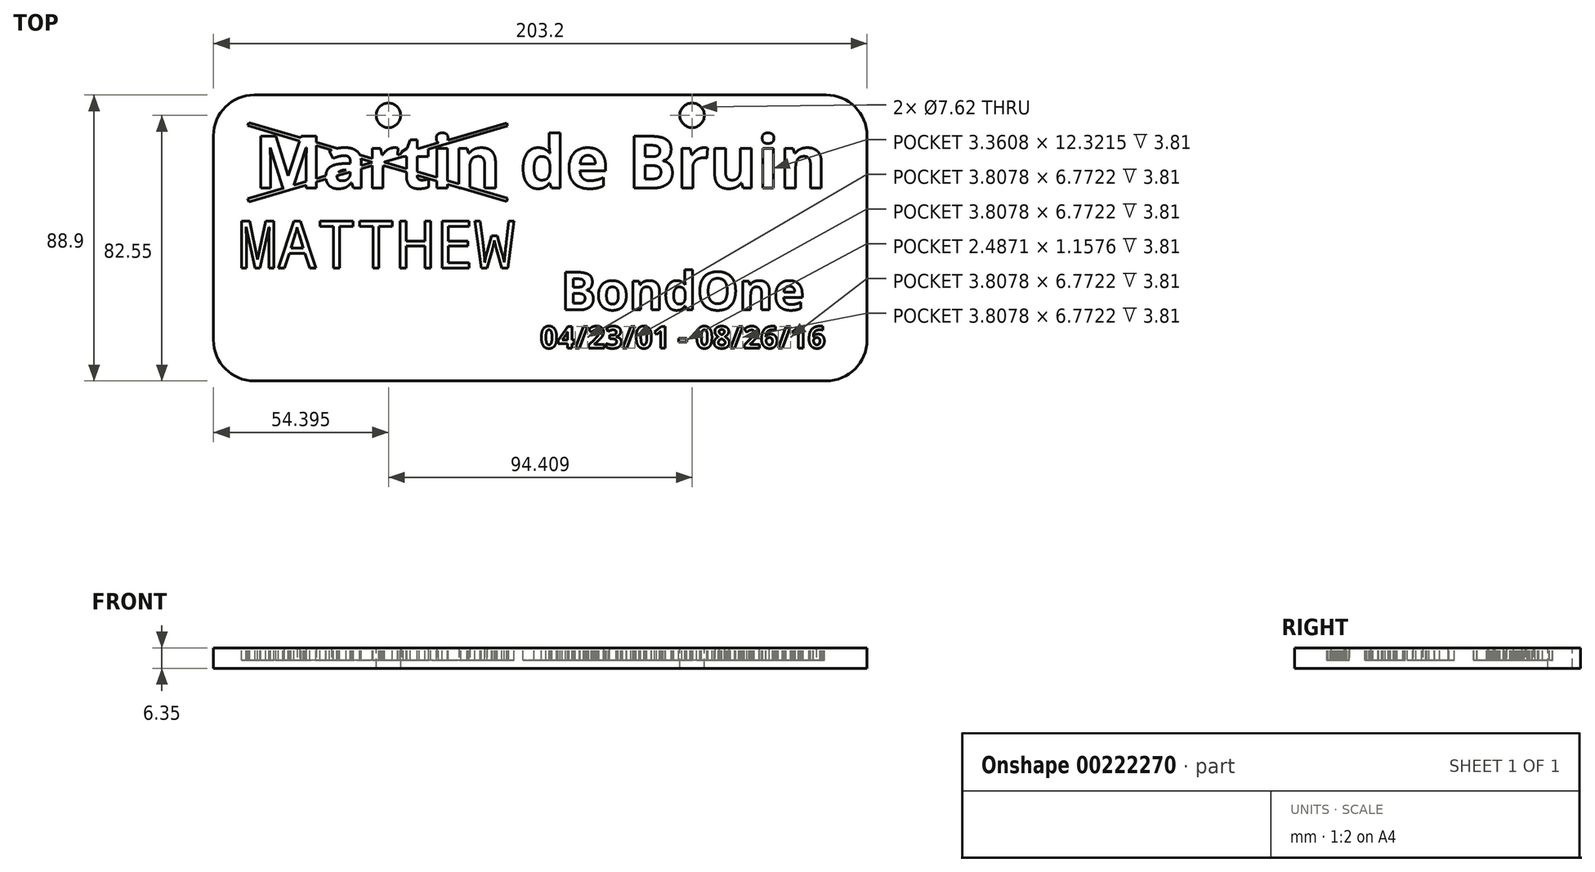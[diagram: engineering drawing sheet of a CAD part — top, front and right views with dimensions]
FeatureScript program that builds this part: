
annotation { "Feature Type Name" : "Feature", "Feature Type Description" : "" }
export const myFeature = defineFeature(function(context is Context, id is Id, definition is map)
    precondition{}
    {
        {
            var Q0;
            Q0=qCreatedBy(makeId("Top.planeOp"),FACE);
            var sketch = newSketch(context, id + "F0", { "sketchPlane" : qUnion([Q0])});
            skLineSegment(sketch, "E0.bottom", {"start": v(-101.6, 44.45) * mm, "end": v(101.6, 44.45) * mm});
            skLineSegment(sketch, "E0.top", {"start": v(-101.6, -44.45) * mm, "end": v(101.6, -44.45) * mm});
            skLineSegment(sketch, "E0.left", {"start": v(-101.6, 44.45) * mm, "end": v(-101.6, -44.45) * mm});
            skLineSegment(sketch, "E0.right", {"start": v(101.6, 44.45) * mm, "end": v(101.6, -44.45) * mm});
            skSolve(sketch);
        }
        {
            var Q0;
            Q0=makeQuery(id+"F0.imprint","IMPRINT",FACE,{"disambiguationData":[TD([[makeQuery(id+"F0.imprint","IMPRINT",EDGE,{"derivedFrom":sQuery(id+"F0.wireOp",EDGE,"E0.bottom")}),-1.0]])]});
            extrude(context, id + "F1", {"entities" : qUnion([Q0]), "depth" : 6.35 * mm});
        }
        {
            var Q0;
            Q0=makeQuery(id+"F1.opExtrude","CAP_FACE",FACE,{"disambiguationData":[OSD([sQuery(id+"F0.wireOp",EDGE,"E0.bottom"),sQuery(id+"F0.wireOp",EDGE,"E0.top"),sQuery(id+"F0.wireOp",EDGE,"E0.left"),sQuery(id+"F0.wireOp",EDGE,"E0.right")])],"isStart":false});
            var sketch = newSketch(context, id + "F2", { "sketchPlane" : qUnion([Q0])});
            skText(sketch, "E1", { "text": "Martin de Bruin", "fontName": "OpenSans-Bold.ttf"});
            skText(sketch, "E2", { "text": "04/23/01 - 08/26/16", "fontName": "OpenSans-Bold.ttf"});
            skText(sketch, "E3", { "text": "MATTHEW", "fontName": "DroidSansMono.ttf"});
            skText(sketch, "E4", { "text": "BondOne", "fontName": "OpenSans-Bold.ttf"});
            const initialGuessF2  = {"E1": [-0.0889, 0.0155, 1, 0, 0.01625], "E2": [0, -0.03429, 1, 0, 0.00683], "E3": [-0.09398, -0.00938, 1, 0, 0.01471], "E4": [0.00635, -0.02238, 1, 0, 0.0118]};
            skSetInitialGuess(sketch, initialGuessF2);
            skSolve(sketch);
        }
        {
            var Q0;
            Q0 = qSketchRegion(id + "F2", true);
            extrude(context, id + "F3", {"entities" : qUnion([Q0]), "operationType" : NewBodyOperationType.REMOVE, "oppositeDirection" : true, "depth" : 3.8 * mm});
        }
        {
            var Q0;
            Q0=makeQuery(id+"F1.opExtrude","SWEPT_EDGE",EDGE,{"disambiguationData":[OSD([sQuery(id+"F0.wireOp",EDGE,"E0.bottom"),sQuery(id+"F0.wireOp",EDGE,"E0.left")])]});
            var Q1;
            Q1=makeQuery(id+"F1.opExtrude","SWEPT_EDGE",EDGE,{"disambiguationData":[OSD([sQuery(id+"F0.wireOp",EDGE,"E0.bottom"),sQuery(id+"F0.wireOp",EDGE,"E0.right")])]});
            var Q2;
            Q2=makeQuery(id+"F1.opExtrude","SWEPT_EDGE",EDGE,{"disambiguationData":[OSD([sQuery(id+"F0.wireOp",EDGE,"E0.top"),sQuery(id+"F0.wireOp",EDGE,"E0.right")])]});
            var Q3;
            Q3=makeQuery(id+"F1.opExtrude","SWEPT_EDGE",EDGE,{"disambiguationData":[OSD([sQuery(id+"F0.wireOp",EDGE,"E0.top"),sQuery(id+"F0.wireOp",EDGE,"E0.left")])]});
            fillet(context, id + "F4", {"entities" : qUnion([Q0, Q1, Q2, Q3]), "radius" : 12.7 * mm, "tangentPropagation" : true, "allowEdgeOverflow" : false});
        }
        {
            var Q0;
            {var subQ0=sQuery(id+"F0.wireOp",EDGE,"E0.top");var subQ1=sQuery(id+"F0.wireOp",EDGE,"E0.left");var subQ2=sQuery(id+"F0.wireOp",EDGE,"E0.bottom");var subQ3=sQuery(id+"F0.wireOp",EDGE,"E0.right");Q0=makeQuery(id+"F3.boolean.opBoolean","SPLIT",FACE,{"disambiguationData":[TD([makeQuery(id+"F1.opExtrude","SWEPT_FACE",FACE,{"disambiguationData":[OSD([subQ2])]})])],"derivedFrom":makeQuery(id+"F1.opExtrude","CAP_FACE",FACE,{"disambiguationData":[OSD([subQ2,subQ0,subQ1,subQ3])],"isStart":false})});}
            var sketch = newSketch(context, id + "F5", { "sketchPlane" : qUnion([Q0])});
            skCircle(sketch, "E5", {"center": v(-47.2, 38.1) * mm, "radius": 3.81 * mm});
            skCircle(sketch, "E6", {"center": v(47.2, 38.1) * mm, "radius": 3.81 * mm});
            skSolve(sketch);
        }
        {
            var Q0;
            Q0=makeQuery(id+"F5.imprint","IMPRINT",FACE,{"disambiguationData":[TD([[makeQuery(id+"F5.imprint","IMPRINT",EDGE,{"derivedFrom":sQuery(id+"F5.wireOp",EDGE,"E5")}),1.0]])]});
            var Q1;
            Q1=makeQuery(id+"F5.imprint","IMPRINT",FACE,{"disambiguationData":[TD([[makeQuery(id+"F5.imprint","IMPRINT",EDGE,{"derivedFrom":sQuery(id+"F5.wireOp",EDGE,"E6")}),1.0]])]});
            extrude(context, id + "F6", {"entities" : qUnion([Q0, Q1]), "operationType" : NewBodyOperationType.REMOVE, "oppositeDirection" : true, "depth" : 25.4 * mm});
        }
        {
            var Q0;
            {var subQ0=sQuery(id+"F0.wireOp",EDGE,"E0.top");var subQ1=sQuery(id+"F0.wireOp",EDGE,"E0.left");var subQ2=sQuery(id+"F0.wireOp",EDGE,"E0.bottom");var subQ3=sQuery(id+"F0.wireOp",EDGE,"E0.right");Q0=makeQuery(id+"F3.boolean.opBoolean","SPLIT",FACE,{"disambiguationData":[TD([makeQuery(id+"F1.opExtrude","SWEPT_FACE",FACE,{"disambiguationData":[OSD([subQ2])]})])],"derivedFrom":makeQuery(id+"F1.opExtrude","CAP_FACE",FACE,{"disambiguationData":[OSD([subQ2,subQ0,subQ1,subQ3])],"isStart":false})});}
            var sketch = newSketch(context, id + "F7", { "sketchPlane" : qUnion([Q0])});
            skLineSegment(sketch, "E7.bottom", {"start": v(-90.93, 35.42) * mm, "end": v(-9.84, 35.42) * mm});
            skLineSegment(sketch, "E7.top", {"start": v(-90.93, 11.69) * mm, "end": v(-9.84, 11.69) * mm});
            skLineSegment(sketch, "E7.left", {"start": v(-90.93, 35.42) * mm, "end": v(-90.93, 11.69) * mm});
            skLineSegment(sketch, "E7.right", {"start": v(-9.84, 35.42) * mm, "end": v(-9.84, 11.69) * mm});
            skLineSegment(sketch, "E8", {"start": v(-90.93, 11.69) * mm, "end": v(-9.84, 35.42) * mm});
            skLineSegment(sketch, "E9", {"start": v(-9.84, 11.69) * mm, "end": v(-90.93, 35.42) * mm});
            skLineSegment(sketch, "E10", {"start": v(-90.93, 12.21) * mm, "end": v(-10.49, 35.76) * mm});
            skLineSegment(sketch, "E11", {"start": v(-10.49, 35.76) * mm, "end": v(-10.2, 34.79) * mm});
            skLineSegment(sketch, "E12", {"start": v(-10.2, 34.79) * mm, "end": v(-90.64, 11.24) * mm});
            skLineSegment(sketch, "E13", {"start": v(-90.64, 11.24) * mm, "end": v(-90.97, 12.34) * mm});
            skLineSegment(sketch, "E14", {"start": v(-90.93, 12.21) * mm, "end": v(-90.93, 12.21) * mm});
            skLineSegment(sketch, "E15", {"start": v(-90.93, 34.9) * mm, "end": v(-10.49, 11.35) * mm});
            skLineSegment(sketch, "E16", {"start": v(-10.49, 11.35) * mm, "end": v(-10.2, 12.32) * mm});
            skLineSegment(sketch, "E17", {"start": v(-10.2, 12.32) * mm, "end": v(-90.64, 35.87) * mm});
            skLineSegment(sketch, "E18", {"start": v(-90.64, 35.87) * mm, "end": v(-90.94, 34.86) * mm});
            skLineSegment(sketch, "E19", {"start": v(-90.93, 34.9) * mm, "end": v(-90.93, 34.9) * mm});
            skSolve(sketch);
        }
        {
            var Q0;
            {var subQ0=sQuery(id+"F7.wireOp",EDGE,"E18");var subQ1=sQuery(id+"F7.wireOp",EDGE,"E7.bottom");var subQ2=makeQuery(id+"F7.imprint","INTERSECT",VERTEX,{"derivedFrom":[subQ1,subQ0]});Q0=makeQuery(id+"F7.imprint","IMPRINT",FACE,{"disambiguationData":[TD([[makeQuery(id+"F7.imprint","IMPRINT",EDGE,{"disambiguationData":[TD([[subQ2,-1.0]])],"derivedFrom":subQ1}),-1.0]])]});}
            var Q1;
            {var subQ0=sQuery(id+"F7.wireOp",EDGE,"E18");var subQ1=sQuery(id+"F7.wireOp",EDGE,"E7.bottom");var subQ2=makeQuery(id+"F7.imprint","INTERSECT",VERTEX,{"derivedFrom":[subQ1,subQ0]});Q1=makeQuery(id+"F7.imprint","IMPRINT",FACE,{"disambiguationData":[TD([[makeQuery(id+"F7.imprint","IMPRINT",EDGE,{"disambiguationData":[TD([[subQ2,-1.0]])],"derivedFrom":subQ1}),1.0]])]});}
            var Q2;
            {var subQ0=sQuery(id+"F7.wireOp",EDGE,"E18");var subQ1=sQuery(id+"F7.wireOp",EDGE,"E9");var subQ2=makeQuery(id+"F7.imprint","INTERSECT",VERTEX,{"derivedFrom":[subQ1,subQ0]});Q2=makeQuery(id+"F7.imprint","IMPRINT",FACE,{"disambiguationData":[TD([[makeQuery(id+"F7.imprint","IMPRINT",EDGE,{"disambiguationData":[TD([[subQ2,1.0]])],"derivedFrom":subQ1}),1.0]])]});}
            var Q3;
            {var subQ0=sQuery(id+"F7.wireOp",EDGE,"E9");var subQ1=makeQuery(id+"F3.boolean.opBoolean","COPY",EDGE,{"derivedFrom":makeQuery(id+"F3.opExtrude","CAP_EDGE",EDGE,{"disambiguationData":[OSD([sQuery(id+"F2.wireOp",EDGE,"E1.sketch_text.stroke-32")])],"isStart":true})});var subQ2=makeQuery(id+"F7.imprint","INTERSECT",VERTEX,{"derivedFrom":[subQ1,subQ0]});Q3=makeQuery(id+"F7.imprint","IMPRINT",FACE,{"disambiguationData":[TD([[makeQuery(id+"F7.imprint","IMPRINT",EDGE,{"disambiguationData":[TD([[subQ2,-1.0]])],"derivedFrom":subQ0}),-1.0]])]});}
            var Q4;
            {var subQ0=sQuery(id+"F7.wireOp",EDGE,"E9");var subQ1=makeQuery(id+"F3.boolean.opBoolean","COPY",EDGE,{"derivedFrom":makeQuery(id+"F3.opExtrude","CAP_EDGE",EDGE,{"disambiguationData":[OSD([sQuery(id+"F2.wireOp",EDGE,"E1.sketch_text.stroke-11")])],"isStart":true})});var subQ2=makeQuery(id+"F7.imprint","INTERSECT",VERTEX,{"derivedFrom":[subQ1,subQ0]});Q4=makeQuery(id+"F7.imprint","IMPRINT",FACE,{"disambiguationData":[TD([[makeQuery(id+"F7.imprint","IMPRINT",EDGE,{"disambiguationData":[TD([[subQ2,-1.0]])],"derivedFrom":subQ0}),-1.0]])]});}
            var Q5;
            {var subQ0=sQuery(id+"F7.wireOp",EDGE,"E9");var subQ1=makeQuery(id+"F3.boolean.opBoolean","COPY",EDGE,{"derivedFrom":makeQuery(id+"F3.opExtrude","CAP_EDGE",EDGE,{"disambiguationData":[OSD([sQuery(id+"F2.wireOp",EDGE,"E1.sketch_text.stroke-11")])],"isStart":true})});var subQ2=makeQuery(id+"F7.imprint","INTERSECT",VERTEX,{"derivedFrom":[subQ1,subQ0]});Q5=makeQuery(id+"F7.imprint","IMPRINT",FACE,{"disambiguationData":[TD([[makeQuery(id+"F7.imprint","IMPRINT",EDGE,{"disambiguationData":[TD([[subQ2,-1.0]])],"derivedFrom":subQ0}),1.0]])]});}
            var Q6;
            {var subQ0=sQuery(id+"F7.wireOp",EDGE,"E9");var subQ1=makeQuery(id+"F3.boolean.opBoolean","COPY",EDGE,{"derivedFrom":makeQuery(id+"F3.opExtrude","CAP_EDGE",EDGE,{"disambiguationData":[OSD([sQuery(id+"F2.wireOp",EDGE,"E1.sketch_text.stroke-32")])],"isStart":true})});var subQ2=makeQuery(id+"F7.imprint","INTERSECT",VERTEX,{"derivedFrom":[subQ1,subQ0]});Q6=makeQuery(id+"F7.imprint","IMPRINT",FACE,{"disambiguationData":[TD([[makeQuery(id+"F7.imprint","IMPRINT",EDGE,{"disambiguationData":[TD([[subQ2,-1.0]])],"derivedFrom":subQ0}),1.0]])]});}
            var Q7;
            {var subQ0=sQuery(id+"F7.wireOp",EDGE,"E9");var subQ1=makeQuery(id+"F3.boolean.opBoolean","COPY",EDGE,{"derivedFrom":makeQuery(id+"F3.opExtrude","CAP_EDGE",EDGE,{"disambiguationData":[OSD([sQuery(id+"F2.wireOp",EDGE,"E1.sketch_text.stroke-34")])],"isStart":true})});var subQ2=makeQuery(id+"F7.imprint","INTERSECT",VERTEX,{"derivedFrom":[subQ1,subQ0]});Q7=makeQuery(id+"F7.imprint","IMPRINT",FACE,{"disambiguationData":[TD([[makeQuery(id+"F7.imprint","IMPRINT",EDGE,{"disambiguationData":[TD([[subQ2,-1.0]])],"derivedFrom":subQ0}),-1.0]])]});}
            var Q8;
            {var subQ0=sQuery(id+"F7.wireOp",EDGE,"E9");var subQ1=makeQuery(id+"F3.boolean.opBoolean","COPY",EDGE,{"derivedFrom":makeQuery(id+"F3.opExtrude","CAP_EDGE",EDGE,{"disambiguationData":[OSD([sQuery(id+"F2.wireOp",EDGE,"E1.sketch_text.stroke-34")])],"isStart":true})});var subQ2=makeQuery(id+"F7.imprint","INTERSECT",VERTEX,{"derivedFrom":[subQ1,subQ0]});Q8=makeQuery(id+"F7.imprint","IMPRINT",FACE,{"disambiguationData":[TD([[makeQuery(id+"F7.imprint","IMPRINT",EDGE,{"disambiguationData":[TD([[subQ2,-1.0]])],"derivedFrom":subQ0}),1.0]])]});}
            var Q9;
            {var subQ0=sQuery(id+"F7.wireOp",EDGE,"E9");var subQ1=makeQuery(id+"F3.boolean.opBoolean","COPY",EDGE,{"derivedFrom":makeQuery(id+"F3.opExtrude","CAP_EDGE",EDGE,{"disambiguationData":[OSD([sQuery(id+"F2.wireOp",EDGE,"E1.sketch_text.stroke-51")])],"isStart":true})});var subQ2=makeQuery(id+"F7.imprint","INTERSECT",VERTEX,{"derivedFrom":[subQ1,subQ0]});Q9=makeQuery(id+"F7.imprint","IMPRINT",FACE,{"disambiguationData":[TD([[makeQuery(id+"F7.imprint","IMPRINT",EDGE,{"disambiguationData":[TD([[subQ2,-1.0]])],"derivedFrom":subQ0}),-1.0]])]});}
            var Q10;
            {var subQ0=sQuery(id+"F7.wireOp",EDGE,"E9");var subQ1=makeQuery(id+"F3.boolean.opBoolean","COPY",EDGE,{"derivedFrom":makeQuery(id+"F3.opExtrude","CAP_EDGE",EDGE,{"disambiguationData":[OSD([sQuery(id+"F2.wireOp",EDGE,"E1.sketch_text.stroke-51")])],"isStart":true})});var subQ2=makeQuery(id+"F7.imprint","INTERSECT",VERTEX,{"derivedFrom":[subQ1,subQ0]});Q10=makeQuery(id+"F7.imprint","IMPRINT",FACE,{"disambiguationData":[TD([[makeQuery(id+"F7.imprint","IMPRINT",EDGE,{"disambiguationData":[TD([[subQ2,-1.0]])],"derivedFrom":subQ0}),1.0]])]});}
            var Q11;
            {var subQ0=sQuery(id+"F7.wireOp",EDGE,"E10");var subQ1=sQuery(id+"F7.wireOp",EDGE,"E9");var subQ2=makeQuery(id+"F7.imprint","INTERSECT",VERTEX,{"derivedFrom":[subQ1,subQ0]});Q11=makeQuery(id+"F7.imprint","IMPRINT",FACE,{"disambiguationData":[TD([[makeQuery(id+"F7.imprint","IMPRINT",EDGE,{"disambiguationData":[TD([[subQ2,-1.0]])],"derivedFrom":subQ1}),-1.0]])]});}
            var Q12;
            {var subQ0=sQuery(id+"F7.wireOp",EDGE,"E9");var subQ1=sQuery(id+"F7.wireOp",EDGE,"E8");var subQ2=makeQuery(id+"F7.imprint","INTERSECT",VERTEX,{"derivedFrom":[subQ1,subQ0]});Q12=makeQuery(id+"F7.imprint","IMPRINT",FACE,{"disambiguationData":[TD([[makeQuery(id+"F7.imprint","IMPRINT",EDGE,{"disambiguationData":[TD([[subQ2,-1.0]])],"derivedFrom":subQ1}),1.0]])]});}
            var Q13;
            {var subQ0=sQuery(id+"F7.wireOp",EDGE,"E9");var subQ1=sQuery(id+"F7.wireOp",EDGE,"E8");var subQ2=makeQuery(id+"F7.imprint","INTERSECT",VERTEX,{"derivedFrom":[subQ1,subQ0]});Q13=makeQuery(id+"F7.imprint","IMPRINT",FACE,{"disambiguationData":[TD([[makeQuery(id+"F7.imprint","IMPRINT",EDGE,{"disambiguationData":[TD([[subQ2,-1.0]])],"derivedFrom":subQ1}),-1.0]])]});}
            var Q14;
            {var subQ0=sQuery(id+"F7.wireOp",EDGE,"E15");var subQ1=sQuery(id+"F7.wireOp",EDGE,"E8");var subQ2=makeQuery(id+"F7.imprint","INTERSECT",VERTEX,{"derivedFrom":[subQ1,subQ0]});Q14=makeQuery(id+"F7.imprint","IMPRINT",FACE,{"disambiguationData":[TD([[makeQuery(id+"F7.imprint","IMPRINT",EDGE,{"disambiguationData":[TD([[subQ2,-1.0]])],"derivedFrom":subQ1}),-1.0]])]});}
            var Q15;
            {var subQ0=sQuery(id+"F7.wireOp",EDGE,"E15");var subQ1=sQuery(id+"F7.wireOp",EDGE,"E8");var subQ2=makeQuery(id+"F7.imprint","INTERSECT",VERTEX,{"derivedFrom":[subQ1,subQ0]});Q15=makeQuery(id+"F7.imprint","IMPRINT",FACE,{"disambiguationData":[TD([[makeQuery(id+"F7.imprint","IMPRINT",EDGE,{"disambiguationData":[TD([[subQ2,-1.0]])],"derivedFrom":subQ1}),1.0]])]});}
            var Q16;
            {var subQ0=sQuery(id+"F7.wireOp",EDGE,"E10");var subQ1=sQuery(id+"F7.wireOp",EDGE,"E9");var subQ2=makeQuery(id+"F7.imprint","INTERSECT",VERTEX,{"derivedFrom":[subQ1,subQ0]});Q16=makeQuery(id+"F7.imprint","IMPRINT",FACE,{"disambiguationData":[TD([[makeQuery(id+"F7.imprint","IMPRINT",EDGE,{"disambiguationData":[TD([[subQ2,-1.0]])],"derivedFrom":subQ1}),1.0]])]});}
            var Q17;
            {var subQ0=sQuery(id+"F7.wireOp",EDGE,"E12");var subQ1=sQuery(id+"F7.wireOp",EDGE,"E9");var subQ2=makeQuery(id+"F7.imprint","INTERSECT",VERTEX,{"derivedFrom":[subQ1,subQ0]});Q17=makeQuery(id+"F7.imprint","IMPRINT",FACE,{"disambiguationData":[TD([[makeQuery(id+"F7.imprint","IMPRINT",EDGE,{"disambiguationData":[TD([[subQ2,1.0]])],"derivedFrom":subQ1}),1.0]])]});}
            var Q18;
            {var subQ0=sQuery(id+"F7.wireOp",EDGE,"E12");var subQ1=sQuery(id+"F7.wireOp",EDGE,"E9");var subQ2=makeQuery(id+"F7.imprint","INTERSECT",VERTEX,{"derivedFrom":[subQ1,subQ0]});Q18=makeQuery(id+"F7.imprint","IMPRINT",FACE,{"disambiguationData":[TD([[makeQuery(id+"F7.imprint","IMPRINT",EDGE,{"disambiguationData":[TD([[subQ2,1.0]])],"derivedFrom":subQ1}),-1.0]])]});}
            var Q19;
            {var subQ0=sQuery(id+"F7.wireOp",EDGE,"E9");var subQ1=makeQuery(id+"F3.boolean.opBoolean","COPY",EDGE,{"derivedFrom":makeQuery(id+"F3.opExtrude","CAP_EDGE",EDGE,{"disambiguationData":[OSD([sQuery(id+"F2.wireOp",EDGE,"E1.sketch_text.stroke-62")])],"isStart":true})});var subQ2=makeQuery(id+"F7.imprint","INTERSECT",VERTEX,{"derivedFrom":[subQ1,subQ0]});Q19=makeQuery(id+"F7.imprint","IMPRINT",FACE,{"disambiguationData":[TD([[makeQuery(id+"F7.imprint","IMPRINT",EDGE,{"disambiguationData":[TD([[subQ2,-1.0]])],"derivedFrom":subQ0}),-1.0]])]});}
            var Q20;
            {var subQ0=sQuery(id+"F7.wireOp",EDGE,"E9");var subQ1=makeQuery(id+"F3.boolean.opBoolean","COPY",EDGE,{"derivedFrom":makeQuery(id+"F3.opExtrude","CAP_EDGE",EDGE,{"disambiguationData":[OSD([sQuery(id+"F2.wireOp",EDGE,"E1.sketch_text.stroke-62")])],"isStart":true})});var subQ2=makeQuery(id+"F7.imprint","INTERSECT",VERTEX,{"derivedFrom":[subQ1,subQ0]});Q20=makeQuery(id+"F7.imprint","IMPRINT",FACE,{"disambiguationData":[TD([[makeQuery(id+"F7.imprint","IMPRINT",EDGE,{"disambiguationData":[TD([[subQ2,-1.0]])],"derivedFrom":subQ0}),1.0]])]});}
            var Q21;
            {var subQ0=sQuery(id+"F7.wireOp",EDGE,"E9");var subQ1=makeQuery(id+"F3.boolean.opBoolean","COPY",EDGE,{"derivedFrom":makeQuery(id+"F3.opExtrude","CAP_EDGE",EDGE,{"disambiguationData":[OSD([sQuery(id+"F2.wireOp",EDGE,"E1.sketch_text.stroke-72")])],"isStart":true})});var subQ2=makeQuery(id+"F7.imprint","INTERSECT",VERTEX,{"derivedFrom":[subQ1,subQ0]});Q21=makeQuery(id+"F7.imprint","IMPRINT",FACE,{"disambiguationData":[TD([[makeQuery(id+"F7.imprint","IMPRINT",EDGE,{"disambiguationData":[TD([[subQ2,-1.0]])],"derivedFrom":subQ0}),-1.0]])]});}
            var Q22;
            {var subQ0=sQuery(id+"F7.wireOp",EDGE,"E9");var subQ1=makeQuery(id+"F3.boolean.opBoolean","COPY",EDGE,{"derivedFrom":makeQuery(id+"F3.opExtrude","CAP_EDGE",EDGE,{"disambiguationData":[OSD([sQuery(id+"F2.wireOp",EDGE,"E1.sketch_text.stroke-72")])],"isStart":true})});var subQ2=makeQuery(id+"F7.imprint","INTERSECT",VERTEX,{"derivedFrom":[subQ1,subQ0]});Q22=makeQuery(id+"F7.imprint","IMPRINT",FACE,{"disambiguationData":[TD([[makeQuery(id+"F7.imprint","IMPRINT",EDGE,{"disambiguationData":[TD([[subQ2,-1.0]])],"derivedFrom":subQ0}),1.0]])]});}
            var Q23;
            {var subQ0=sQuery(id+"F7.wireOp",EDGE,"E9");var subQ1=makeQuery(id+"F3.boolean.opBoolean","COPY",EDGE,{"derivedFrom":makeQuery(id+"F3.opExtrude","CAP_EDGE",EDGE,{"disambiguationData":[OSD([sQuery(id+"F2.wireOp",EDGE,"E1.sketch_text.stroke-81")])],"isStart":true})});var subQ2=makeQuery(id+"F7.imprint","INTERSECT",VERTEX,{"derivedFrom":[subQ1,subQ0]});Q23=makeQuery(id+"F7.imprint","IMPRINT",FACE,{"disambiguationData":[TD([[makeQuery(id+"F7.imprint","IMPRINT",EDGE,{"disambiguationData":[TD([[subQ2,-1.0]])],"derivedFrom":subQ0}),-1.0]])]});}
            var Q24;
            {var subQ0=sQuery(id+"F7.wireOp",EDGE,"E9");var subQ1=makeQuery(id+"F3.boolean.opBoolean","COPY",EDGE,{"derivedFrom":makeQuery(id+"F3.opExtrude","CAP_EDGE",EDGE,{"disambiguationData":[OSD([sQuery(id+"F2.wireOp",EDGE,"E1.sketch_text.stroke-81")])],"isStart":true})});var subQ2=makeQuery(id+"F7.imprint","INTERSECT",VERTEX,{"derivedFrom":[subQ1,subQ0]});Q24=makeQuery(id+"F7.imprint","IMPRINT",FACE,{"disambiguationData":[TD([[makeQuery(id+"F7.imprint","IMPRINT",EDGE,{"disambiguationData":[TD([[subQ2,-1.0]])],"derivedFrom":subQ0}),1.0]])]});}
            var Q25;
            {var subQ0=sQuery(id+"F7.wireOp",EDGE,"E9");var subQ1=makeQuery(id+"F3.boolean.opBoolean","COPY",EDGE,{"derivedFrom":makeQuery(id+"F3.opExtrude","CAP_EDGE",EDGE,{"disambiguationData":[OSD([sQuery(id+"F2.wireOp",EDGE,"E1.sketch_text.stroke-83")])],"isStart":true})});var subQ2=makeQuery(id+"F7.imprint","INTERSECT",VERTEX,{"derivedFrom":[subQ1,subQ0]});Q25=makeQuery(id+"F7.imprint","IMPRINT",FACE,{"disambiguationData":[TD([[makeQuery(id+"F7.imprint","IMPRINT",EDGE,{"disambiguationData":[TD([[subQ2,-1.0]])],"derivedFrom":subQ0}),-1.0]])]});}
            var Q26;
            {var subQ0=sQuery(id+"F7.wireOp",EDGE,"E9");var subQ1=makeQuery(id+"F3.boolean.opBoolean","COPY",EDGE,{"derivedFrom":makeQuery(id+"F3.opExtrude","CAP_EDGE",EDGE,{"disambiguationData":[OSD([sQuery(id+"F2.wireOp",EDGE,"E1.sketch_text.stroke-83")])],"isStart":true})});var subQ2=makeQuery(id+"F7.imprint","INTERSECT",VERTEX,{"derivedFrom":[subQ1,subQ0]});Q26=makeQuery(id+"F7.imprint","IMPRINT",FACE,{"disambiguationData":[TD([[makeQuery(id+"F7.imprint","IMPRINT",EDGE,{"disambiguationData":[TD([[subQ2,-1.0]])],"derivedFrom":subQ0}),1.0]])]});}
            var Q27;
            {var subQ0=sQuery(id+"F7.wireOp",EDGE,"E9");var subQ1=makeQuery(id+"F3.boolean.opBoolean","COPY",EDGE,{"derivedFrom":makeQuery(id+"F3.opExtrude","CAP_EDGE",EDGE,{"disambiguationData":[OSD([sQuery(id+"F2.wireOp",EDGE,"E1.sketch_text.stroke-92")])],"isStart":true})});var subQ2=makeQuery(id+"F7.imprint","INTERSECT",VERTEX,{"derivedFrom":[subQ1,subQ0]});Q27=makeQuery(id+"F7.imprint","IMPRINT",FACE,{"disambiguationData":[TD([[makeQuery(id+"F7.imprint","IMPRINT",EDGE,{"disambiguationData":[TD([[subQ2,-1.0]])],"derivedFrom":subQ0}),-1.0]])]});}
            var Q28;
            {var subQ0=sQuery(id+"F7.wireOp",EDGE,"E9");var subQ1=makeQuery(id+"F3.boolean.opBoolean","COPY",EDGE,{"derivedFrom":makeQuery(id+"F3.opExtrude","CAP_EDGE",EDGE,{"disambiguationData":[OSD([sQuery(id+"F2.wireOp",EDGE,"E1.sketch_text.stroke-92")])],"isStart":true})});var subQ2=makeQuery(id+"F7.imprint","INTERSECT",VERTEX,{"derivedFrom":[subQ1,subQ0]});Q28=makeQuery(id+"F7.imprint","IMPRINT",FACE,{"disambiguationData":[TD([[makeQuery(id+"F7.imprint","IMPRINT",EDGE,{"disambiguationData":[TD([[subQ2,-1.0]])],"derivedFrom":subQ0}),1.0]])]});}
            var Q29;
            {var subQ0=makeQuery(id+"F3.boolean.opBoolean","COPY",EDGE,{"derivedFrom":makeQuery(id+"F3.opExtrude","CAP_EDGE",EDGE,{"disambiguationData":[OSD([sQuery(id+"F2.wireOp",EDGE,"E1.sketch_text.stroke-91")])],"isStart":true})});var subQ3=sQuery(id+"F7.wireOp",EDGE,"E9");var subQ4=makeQuery(id+"F7.imprint","INTERSECT",VERTEX,{"derivedFrom":[subQ0,subQ3]});Q29=makeQuery(id+"F7.imprint","IMPRINT",FACE,{"disambiguationData":[TD([[makeQuery(id+"F7.imprint","IMPRINT",EDGE,{"disambiguationData":[TD([[subQ4,-1.0]])],"derivedFrom":subQ3}),-1.0]])]});}
            var Q30;
            {var subQ0=sQuery(id+"F7.wireOp",EDGE,"E9");var subQ1=makeQuery(id+"F3.boolean.opBoolean","COPY",EDGE,{"derivedFrom":makeQuery(id+"F3.opExtrude","CAP_EDGE",EDGE,{"disambiguationData":[OSD([sQuery(id+"F2.wireOp",EDGE,"E1.sketch_text.stroke-91")])],"isStart":true})});var subQ2=makeQuery(id+"F7.imprint","INTERSECT",VERTEX,{"derivedFrom":[subQ1,subQ0]});Q30=makeQuery(id+"F7.imprint","IMPRINT",FACE,{"disambiguationData":[TD([[makeQuery(id+"F7.imprint","IMPRINT",EDGE,{"disambiguationData":[TD([[subQ2,-1.0]])],"derivedFrom":subQ0}),1.0]])]});}
            var Q31;
            {var subQ0=sQuery(id+"F7.wireOp",EDGE,"E15");var subQ1=sQuery(id+"F7.wireOp",EDGE,"E7.top");var subQ2=makeQuery(id+"F7.imprint","INTERSECT",VERTEX,{"derivedFrom":[subQ1,subQ0]});Q31=makeQuery(id+"F7.imprint","IMPRINT",FACE,{"disambiguationData":[TD([[makeQuery(id+"F7.imprint","IMPRINT",EDGE,{"disambiguationData":[TD([[subQ2,-1.0]])],"derivedFrom":subQ1}),1.0]])]});}
            var Q32;
            {var subQ5=sQuery(id+"F7.wireOp",EDGE,"E16");var subQ7=sQuery(id+"F7.wireOp",EDGE,"E9");var subQ8=makeQuery(id+"F7.imprint","INTERSECT",VERTEX,{"derivedFrom":[subQ7,subQ5]});Q32=makeQuery(id+"F7.imprint","IMPRINT",FACE,{"disambiguationData":[TD([[makeQuery(id+"F7.imprint","IMPRINT",EDGE,{"disambiguationData":[TD([[subQ8,-1.0]])],"derivedFrom":subQ7}),-1.0]])]});}
            var Q33;
            {var subQ0=sQuery(id+"F7.wireOp",EDGE,"E15");var subQ1=sQuery(id+"F7.wireOp",EDGE,"E7.top");var subQ2=makeQuery(id+"F7.imprint","INTERSECT",VERTEX,{"derivedFrom":[subQ1,subQ0]});Q33=makeQuery(id+"F7.imprint","IMPRINT",FACE,{"disambiguationData":[TD([[makeQuery(id+"F7.imprint","IMPRINT",EDGE,{"disambiguationData":[TD([[subQ2,-1.0]])],"derivedFrom":subQ1}),-1.0]])]});}
            var Q34;
            {var subQ1=sQuery(id+"F7.wireOp",EDGE,"E7.bottom");var subQ5=sQuery(id+"F7.wireOp",EDGE,"E10");var subQ6=makeQuery(id+"F7.imprint","INTERSECT",VERTEX,{"derivedFrom":[subQ1,subQ5]});Q34=makeQuery(id+"F7.imprint","IMPRINT",FACE,{"disambiguationData":[TD([[makeQuery(id+"F7.imprint","IMPRINT",EDGE,{"disambiguationData":[TD([[subQ6,-1.0]])],"derivedFrom":subQ1}),-1.0]])]});}
            var Q35;
            {var subQ5=sQuery(id+"F7.wireOp",EDGE,"E8");var subQ7=makeQuery(id+"F3.boolean.opBoolean","COPY",EDGE,{"derivedFrom":makeQuery(id+"F3.opExtrude","CAP_EDGE",EDGE,{"disambiguationData":[OSD([sQuery(id+"F2.wireOp",EDGE,"E1.sketch_text.stroke-69")])],"isStart":true})});var subQ11=makeQuery(id+"F7.imprint","INTERSECT",VERTEX,{"derivedFrom":[subQ7,subQ5]});Q35=makeQuery(id+"F7.imprint","IMPRINT",FACE,{"disambiguationData":[TD([[makeQuery(id+"F7.imprint","IMPRINT",EDGE,{"disambiguationData":[TD([[subQ11,-1.0]])],"derivedFrom":subQ5}),-1.0]])]});}
            var Q36;
            {var subQ0=sQuery(id+"F7.wireOp",EDGE,"E10");var subQ1=sQuery(id+"F7.wireOp",EDGE,"E7.bottom");var subQ2=makeQuery(id+"F7.imprint","INTERSECT",VERTEX,{"derivedFrom":[subQ1,subQ0]});Q36=makeQuery(id+"F7.imprint","IMPRINT",FACE,{"disambiguationData":[TD([[makeQuery(id+"F7.imprint","IMPRINT",EDGE,{"disambiguationData":[TD([[subQ2,-1.0]])],"derivedFrom":subQ1}),1.0]])]});}
            var Q37;
            {var subQ0=sQuery(id+"F7.wireOp",EDGE,"E8");var subQ1=makeQuery(id+"F3.boolean.opBoolean","COPY",EDGE,{"derivedFrom":makeQuery(id+"F3.opExtrude","CAP_EDGE",EDGE,{"disambiguationData":[OSD([sQuery(id+"F2.wireOp",EDGE,"E1.sketch_text.stroke-79")])],"isStart":true})});var subQ2=makeQuery(id+"F7.imprint","INTERSECT",VERTEX,{"derivedFrom":[subQ1,subQ0]});Q37=makeQuery(id+"F7.imprint","IMPRINT",FACE,{"disambiguationData":[TD([[makeQuery(id+"F7.imprint","IMPRINT",EDGE,{"disambiguationData":[TD([[subQ2,-1.0]])],"derivedFrom":subQ0}),-1.0]])]});}
            var Q38;
            {var subQ5=makeQuery(id+"F3.boolean.opBoolean","COPY",EDGE,{"derivedFrom":makeQuery(id+"F3.opExtrude","CAP_EDGE",EDGE,{"disambiguationData":[OSD([sQuery(id+"F2.wireOp",EDGE,"E1.sketch_text.stroke-79")])],"isStart":true})});var subQ7=sQuery(id+"F7.wireOp",EDGE,"E8");var subQ8=makeQuery(id+"F7.imprint","INTERSECT",VERTEX,{"derivedFrom":[subQ5,subQ7]});Q38=makeQuery(id+"F7.imprint","IMPRINT",FACE,{"disambiguationData":[TD([[makeQuery(id+"F7.imprint","IMPRINT",EDGE,{"disambiguationData":[TD([[subQ8,-1.0]])],"derivedFrom":subQ7}),1.0]])]});}
            var Q39;
            {var subQ0=sQuery(id+"F7.wireOp",EDGE,"E13");var subQ1=sQuery(id+"F7.wireOp",EDGE,"E8");var subQ2=makeQuery(id+"F7.imprint","INTERSECT",VERTEX,{"derivedFrom":[subQ1,subQ0]});Q39=makeQuery(id+"F7.imprint","IMPRINT",FACE,{"disambiguationData":[TD([[makeQuery(id+"F7.imprint","IMPRINT",EDGE,{"disambiguationData":[TD([[subQ2,-1.0]])],"derivedFrom":subQ1}),1.0]])]});}
            var Q40;
            {var subQ1=sQuery(id+"F7.wireOp",EDGE,"E7.top");var subQ9=sQuery(id+"F7.wireOp",EDGE,"E13");var subQ14=makeQuery(id+"F7.imprint","INTERSECT",VERTEX,{"derivedFrom":[subQ1,subQ9]});Q40=makeQuery(id+"F7.imprint","IMPRINT",FACE,{"disambiguationData":[TD([[makeQuery(id+"F7.imprint","IMPRINT",EDGE,{"disambiguationData":[TD([[subQ14,-1.0]])],"derivedFrom":subQ1}),1.0]])]});}
            var Q41;
            {var subQ0=sQuery(id+"F7.wireOp",EDGE,"E13");var subQ1=sQuery(id+"F7.wireOp",EDGE,"E7.top");var subQ2=makeQuery(id+"F7.imprint","INTERSECT",VERTEX,{"derivedFrom":[subQ1,subQ0]});Q41=makeQuery(id+"F7.imprint","IMPRINT",FACE,{"disambiguationData":[TD([[makeQuery(id+"F7.imprint","IMPRINT",EDGE,{"disambiguationData":[TD([[subQ2,-1.0]])],"derivedFrom":subQ1}),-1.0]])]});}
            var Q42;
            {var subQ0=sQuery(id+"F7.wireOp",EDGE,"E8");var subQ1=makeQuery(id+"F3.boolean.opBoolean","COPY",EDGE,{"derivedFrom":makeQuery(id+"F3.opExtrude","CAP_EDGE",EDGE,{"disambiguationData":[OSD([sQuery(id+"F2.wireOp",EDGE,"E1.sketch_text.stroke-18")])],"isStart":true})});var subQ2=makeQuery(id+"F7.imprint","INTERSECT",VERTEX,{"derivedFrom":[subQ1,subQ0]});Q42=makeQuery(id+"F7.imprint","IMPRINT",FACE,{"disambiguationData":[TD([[makeQuery(id+"F7.imprint","IMPRINT",EDGE,{"disambiguationData":[TD([[subQ2,-1.0]])],"derivedFrom":subQ0}),1.0]])]});}
            var Q43;
            {var subQ0=sQuery(id+"F7.wireOp",EDGE,"E8");var subQ1=makeQuery(id+"F3.boolean.opBoolean","COPY",EDGE,{"derivedFrom":makeQuery(id+"F3.opExtrude","CAP_EDGE",EDGE,{"disambiguationData":[OSD([sQuery(id+"F2.wireOp",EDGE,"E1.sketch_text.stroke-18")])],"isStart":true})});var subQ2=makeQuery(id+"F7.imprint","INTERSECT",VERTEX,{"derivedFrom":[subQ1,subQ0]});Q43=makeQuery(id+"F7.imprint","IMPRINT",FACE,{"disambiguationData":[TD([[makeQuery(id+"F7.imprint","IMPRINT",EDGE,{"disambiguationData":[TD([[subQ2,-1.0]])],"derivedFrom":subQ0}),-1.0]])]});}
            var Q44;
            {var subQ0=sQuery(id+"F7.wireOp",EDGE,"E8");var subQ1=makeQuery(id+"F3.boolean.opBoolean","COPY",EDGE,{"derivedFrom":makeQuery(id+"F3.opExtrude","CAP_EDGE",EDGE,{"disambiguationData":[OSD([sQuery(id+"F2.wireOp",EDGE,"E1.sketch_text.stroke-17")])],"isStart":true})});var subQ2=makeQuery(id+"F7.imprint","INTERSECT",VERTEX,{"derivedFrom":[subQ1,subQ0]});Q44=makeQuery(id+"F7.imprint","IMPRINT",FACE,{"disambiguationData":[TD([[makeQuery(id+"F7.imprint","IMPRINT",EDGE,{"disambiguationData":[TD([[subQ2,-1.0]])],"derivedFrom":subQ0}),1.0]])]});}
            var Q45;
            {var subQ0=sQuery(id+"F7.wireOp",EDGE,"E8");var subQ1=makeQuery(id+"F3.boolean.opBoolean","COPY",EDGE,{"derivedFrom":makeQuery(id+"F3.opExtrude","CAP_EDGE",EDGE,{"disambiguationData":[OSD([sQuery(id+"F2.wireOp",EDGE,"E1.sketch_text.stroke-13")])],"isStart":true})});var subQ2=makeQuery(id+"F7.imprint","INTERSECT",VERTEX,{"derivedFrom":[subQ1,subQ0]});Q45=makeQuery(id+"F7.imprint","IMPRINT",FACE,{"disambiguationData":[TD([[makeQuery(id+"F7.imprint","IMPRINT",EDGE,{"disambiguationData":[TD([[subQ2,-1.0]])],"derivedFrom":subQ0}),-1.0]])]});}
            var Q46;
            {var subQ0=sQuery(id+"F7.wireOp",EDGE,"E8");var subQ1=makeQuery(id+"F3.boolean.opBoolean","COPY",EDGE,{"derivedFrom":makeQuery(id+"F3.opExtrude","CAP_EDGE",EDGE,{"disambiguationData":[OSD([sQuery(id+"F2.wireOp",EDGE,"E1.sketch_text.stroke-13")])],"isStart":true})});var subQ2=makeQuery(id+"F7.imprint","INTERSECT",VERTEX,{"derivedFrom":[subQ1,subQ0]});Q46=makeQuery(id+"F7.imprint","IMPRINT",FACE,{"disambiguationData":[TD([[makeQuery(id+"F7.imprint","IMPRINT",EDGE,{"disambiguationData":[TD([[subQ2,-1.0]])],"derivedFrom":subQ0}),1.0]])]});}
            var Q47;
            {var subQ3=sQuery(id+"F7.wireOp",EDGE,"E8");var subQ7=makeQuery(id+"F3.boolean.opBoolean","COPY",EDGE,{"derivedFrom":makeQuery(id+"F3.opExtrude","CAP_EDGE",EDGE,{"disambiguationData":[OSD([sQuery(id+"F2.wireOp",EDGE,"E1.sketch_text.stroke-11")])],"isStart":true})});var subQ9=makeQuery(id+"F7.imprint","INTERSECT",VERTEX,{"derivedFrom":[subQ7,subQ3]});Q47=makeQuery(id+"F7.imprint","IMPRINT",FACE,{"disambiguationData":[TD([[makeQuery(id+"F7.imprint","IMPRINT",EDGE,{"disambiguationData":[TD([[subQ9,-1.0]])],"derivedFrom":subQ3}),1.0]])]});}
            var Q48;
            {var subQ0=sQuery(id+"F7.wireOp",EDGE,"E8");var subQ1=makeQuery(id+"F3.boolean.opBoolean","COPY",EDGE,{"derivedFrom":makeQuery(id+"F3.opExtrude","CAP_EDGE",EDGE,{"disambiguationData":[OSD([sQuery(id+"F2.wireOp",EDGE,"E1.sketch_text.stroke-11")])],"isStart":true})});var subQ2=makeQuery(id+"F7.imprint","INTERSECT",VERTEX,{"derivedFrom":[subQ1,subQ0]});Q48=makeQuery(id+"F7.imprint","IMPRINT",FACE,{"disambiguationData":[TD([[makeQuery(id+"F7.imprint","IMPRINT",EDGE,{"disambiguationData":[TD([[subQ2,-1.0]])],"derivedFrom":subQ0}),-1.0]])]});}
            var Q49;
            {var subQ0=sQuery(id+"F7.wireOp",EDGE,"E8");var subQ1=makeQuery(id+"F3.boolean.opBoolean","COPY",EDGE,{"derivedFrom":makeQuery(id+"F3.opExtrude","CAP_EDGE",EDGE,{"disambiguationData":[OSD([sQuery(id+"F2.wireOp",EDGE,"E1.sketch_text.stroke-24")])],"isStart":true})});var subQ2=makeQuery(id+"F7.imprint","INTERSECT",VERTEX,{"derivedFrom":[subQ1,subQ0]});Q49=makeQuery(id+"F7.imprint","IMPRINT",FACE,{"disambiguationData":[TD([[makeQuery(id+"F7.imprint","IMPRINT",EDGE,{"disambiguationData":[TD([[subQ2,-1.0]])],"derivedFrom":subQ0}),-1.0]])]});}
            var Q50;
            {var subQ1=makeQuery(id+"F3.boolean.opBoolean","COPY",EDGE,{"derivedFrom":makeQuery(id+"F3.opExtrude","CAP_EDGE",EDGE,{"disambiguationData":[OSD([sQuery(id+"F2.wireOp",EDGE,"E1.sketch_text.stroke-24")])],"isStart":true})});var subQ5=sQuery(id+"F7.wireOp",EDGE,"E8");var subQ6=makeQuery(id+"F7.imprint","INTERSECT",VERTEX,{"derivedFrom":[subQ1,subQ5]});Q50=makeQuery(id+"F7.imprint","IMPRINT",FACE,{"disambiguationData":[TD([[makeQuery(id+"F7.imprint","IMPRINT",EDGE,{"disambiguationData":[TD([[subQ6,-1.0]])],"derivedFrom":subQ5}),1.0]])]});}
            var Q51;
            {var subQ0=sQuery(id+"F7.wireOp",EDGE,"E8");var subQ1=makeQuery(id+"F3.boolean.opBoolean","COPY",EDGE,{"derivedFrom":makeQuery(id+"F3.opExtrude","CAP_EDGE",EDGE,{"disambiguationData":[OSD([sQuery(id+"F2.wireOp",EDGE,"E1.sketch_text.stroke-35")])],"isStart":true})});var subQ2=makeQuery(id+"F7.imprint","INTERSECT",VERTEX,{"derivedFrom":[subQ1,subQ0]});Q51=makeQuery(id+"F7.imprint","IMPRINT",FACE,{"disambiguationData":[TD([[makeQuery(id+"F7.imprint","IMPRINT",EDGE,{"disambiguationData":[TD([[subQ2,-1.0]])],"derivedFrom":subQ0}),-1.0]])]});}
            var Q52;
            {var subQ0=sQuery(id+"F7.wireOp",EDGE,"E8");var subQ1=makeQuery(id+"F3.boolean.opBoolean","COPY",EDGE,{"derivedFrom":makeQuery(id+"F3.opExtrude","CAP_EDGE",EDGE,{"disambiguationData":[OSD([sQuery(id+"F2.wireOp",EDGE,"E1.sketch_text.stroke-35")])],"isStart":true})});var subQ2=makeQuery(id+"F7.imprint","INTERSECT",VERTEX,{"derivedFrom":[subQ1,subQ0]});Q52=makeQuery(id+"F7.imprint","IMPRINT",FACE,{"disambiguationData":[TD([[makeQuery(id+"F7.imprint","IMPRINT",EDGE,{"disambiguationData":[TD([[subQ2,-1.0]])],"derivedFrom":subQ0}),1.0]])]});}
            var Q53;
            {var subQ0=sQuery(id+"F7.wireOp",EDGE,"E15");var subQ1=sQuery(id+"F7.wireOp",EDGE,"E8");var subQ2=makeQuery(id+"F7.imprint","INTERSECT",VERTEX,{"derivedFrom":[subQ1,subQ0]});Q53=makeQuery(id+"F7.imprint","IMPRINT",FACE,{"disambiguationData":[TD([[makeQuery(id+"F7.imprint","IMPRINT",EDGE,{"disambiguationData":[TD([[subQ2,1.0]])],"derivedFrom":subQ1}),-1.0]])]});}
            var Q54;
            {var subQ0=sQuery(id+"F7.wireOp",EDGE,"E15");var subQ1=sQuery(id+"F7.wireOp",EDGE,"E8");var subQ2=makeQuery(id+"F7.imprint","INTERSECT",VERTEX,{"derivedFrom":[subQ1,subQ0]});Q54=makeQuery(id+"F7.imprint","IMPRINT",FACE,{"disambiguationData":[TD([[makeQuery(id+"F7.imprint","IMPRINT",EDGE,{"disambiguationData":[TD([[subQ2,1.0]])],"derivedFrom":subQ1}),1.0]])]});}
            var Q55;
            {var subQ0=sQuery(id+"F7.wireOp",EDGE,"E17");var subQ1=sQuery(id+"F7.wireOp",EDGE,"E8");var subQ2=makeQuery(id+"F7.imprint","INTERSECT",VERTEX,{"derivedFrom":[subQ1,subQ0]});Q55=makeQuery(id+"F7.imprint","IMPRINT",FACE,{"disambiguationData":[TD([[makeQuery(id+"F7.imprint","IMPRINT",EDGE,{"disambiguationData":[TD([[subQ2,-1.0]])],"derivedFrom":subQ1}),1.0]])]});}
            var Q56;
            {var subQ3=sQuery(id+"F7.wireOp",EDGE,"E8");var subQ5=sQuery(id+"F7.wireOp",EDGE,"E17");var subQ6=makeQuery(id+"F7.imprint","INTERSECT",VERTEX,{"derivedFrom":[subQ3,subQ5]});Q56=makeQuery(id+"F7.imprint","IMPRINT",FACE,{"disambiguationData":[TD([[makeQuery(id+"F7.imprint","IMPRINT",EDGE,{"disambiguationData":[TD([[subQ6,-1.0]])],"derivedFrom":subQ3}),-1.0]])]});}
            var Q57;
            {var subQ5=makeQuery(id+"F3.boolean.opBoolean","COPY",EDGE,{"derivedFrom":makeQuery(id+"F3.opExtrude","CAP_EDGE",EDGE,{"disambiguationData":[OSD([sQuery(id+"F2.wireOp",EDGE,"E1.sketch_text.stroke-46")])],"isStart":true})});Q57=makeQuery(id+"F7.imprint","IMPRINT",FACE,{"disambiguationData":[TD([[makeQuery(id+"F7.imprint","IMPRINT",EDGE,{"derivedFrom":subQ5}),-1.0]])]});}
            var Q58;
            {var subQ0=sQuery(id+"F7.wireOp",EDGE,"E8");var subQ1=makeQuery(id+"F3.boolean.opBoolean","COPY",EDGE,{"derivedFrom":makeQuery(id+"F3.opExtrude","CAP_EDGE",EDGE,{"disambiguationData":[OSD([sQuery(id+"F2.wireOp",EDGE,"E1.sketch_text.stroke-45")])],"isStart":true})});var subQ2=makeQuery(id+"F7.imprint","INTERSECT",VERTEX,{"derivedFrom":[subQ1,subQ0]});Q58=makeQuery(id+"F7.imprint","IMPRINT",FACE,{"disambiguationData":[TD([[makeQuery(id+"F7.imprint","IMPRINT",EDGE,{"disambiguationData":[TD([[subQ2,-1.0]])],"derivedFrom":subQ0}),1.0]])]});}
            var Q59;
            {var subQ0=makeQuery(id+"F3.boolean.opBoolean","COPY",EDGE,{"derivedFrom":makeQuery(id+"F3.opExtrude","CAP_EDGE",EDGE,{"disambiguationData":[OSD([sQuery(id+"F2.wireOp",EDGE,"E1.sketch_text.stroke-46")])],"isStart":true})});Q59=makeQuery(id+"F7.imprint","IMPRINT",FACE,{"disambiguationData":[TD([[makeQuery(id+"F7.imprint","IMPRINT",EDGE,{"derivedFrom":subQ0}),1.0]])]});}
            var Q60;
            {var subQ0=makeQuery(id+"F3.boolean.opBoolean","COPY",EDGE,{"derivedFrom":makeQuery(id+"F3.opExtrude","CAP_EDGE",EDGE,{"disambiguationData":[OSD([sQuery(id+"F2.wireOp",EDGE,"E1.sketch_text.stroke-64")])],"isStart":true})});var subQ8=sQuery(id+"F7.wireOp",EDGE,"E8");var subQ11=makeQuery(id+"F7.imprint","INTERSECT",VERTEX,{"derivedFrom":[subQ0,subQ8]});Q60=makeQuery(id+"F7.imprint","IMPRINT",FACE,{"disambiguationData":[TD([[makeQuery(id+"F7.imprint","IMPRINT",EDGE,{"disambiguationData":[TD([[subQ11,-1.0]])],"derivedFrom":subQ8}),-1.0]])]});}
            var Q61;
            {var subQ0=sQuery(id+"F7.wireOp",EDGE,"E8");var subQ1=makeQuery(id+"F3.boolean.opBoolean","COPY",EDGE,{"derivedFrom":makeQuery(id+"F3.opExtrude","CAP_EDGE",EDGE,{"disambiguationData":[OSD([sQuery(id+"F2.wireOp",EDGE,"E1.sketch_text.stroke-64")])],"isStart":true})});var subQ2=makeQuery(id+"F7.imprint","INTERSECT",VERTEX,{"derivedFrom":[subQ1,subQ0]});Q61=makeQuery(id+"F7.imprint","IMPRINT",FACE,{"disambiguationData":[TD([[makeQuery(id+"F7.imprint","IMPRINT",EDGE,{"disambiguationData":[TD([[subQ2,-1.0]])],"derivedFrom":subQ0}),1.0]])]});}
            var Q62;
            {var subQ0=sQuery(id+"F7.wireOp",EDGE,"E8");var subQ1=makeQuery(id+"F3.boolean.opBoolean","COPY",EDGE,{"derivedFrom":makeQuery(id+"F3.opExtrude","CAP_EDGE",EDGE,{"disambiguationData":[OSD([sQuery(id+"F2.wireOp",EDGE,"E1.sketch_text.stroke-69")])],"isStart":true})});var subQ2=makeQuery(id+"F7.imprint","INTERSECT",VERTEX,{"derivedFrom":[subQ1,subQ0]});Q62=makeQuery(id+"F7.imprint","IMPRINT",FACE,{"disambiguationData":[TD([[makeQuery(id+"F7.imprint","IMPRINT",EDGE,{"disambiguationData":[TD([[subQ2,-1.0]])],"derivedFrom":subQ0}),1.0]])]});}
            var Q63;
            {var subQ0=sQuery(id+"F7.wireOp",EDGE,"E8");var subQ1=makeQuery(id+"F3.boolean.opBoolean","COPY",EDGE,{"derivedFrom":makeQuery(id+"F3.opExtrude","CAP_EDGE",EDGE,{"disambiguationData":[OSD([sQuery(id+"F2.wireOp",EDGE,"E1.sketch_text.stroke-47")])],"isStart":true})});var subQ2=makeQuery(id+"F7.imprint","INTERSECT",VERTEX,{"disambiguationData":[OD(0.0)],"derivedFrom":[subQ1,subQ0]});Q63=makeQuery(id+"F7.imprint","IMPRINT",FACE,{"disambiguationData":[TD([[makeQuery(id+"F7.imprint","IMPRINT",EDGE,{"disambiguationData":[TD([[subQ2,-1.0]])],"derivedFrom":subQ0}),1.0]])]});}
            extrude(context, id + "F8", {"entities" : qUnion([Q0, Q1, Q2, Q3, Q4, Q5, Q6, Q7, Q8, Q9, Q10, Q11, Q12, Q13, Q14, Q15, Q16, Q17, Q18, Q19, Q20, Q21, Q22, Q23, Q24, Q25, Q26, Q27, Q28, Q29, Q30, Q31, Q32, Q33, Q34, Q35, Q36, Q37, Q38, Q39, Q40, Q41, Q42, Q43, Q44, Q45, Q46, Q47, Q48, Q49, Q50, Q51, Q52, Q53, Q54, Q55, Q56, Q57, Q58, Q59, Q60, Q61, Q62, Q63]), "operationType" : NewBodyOperationType.REMOVE, "oppositeDirection" : true, "depth" : 3.8 * mm});
        }
    });
